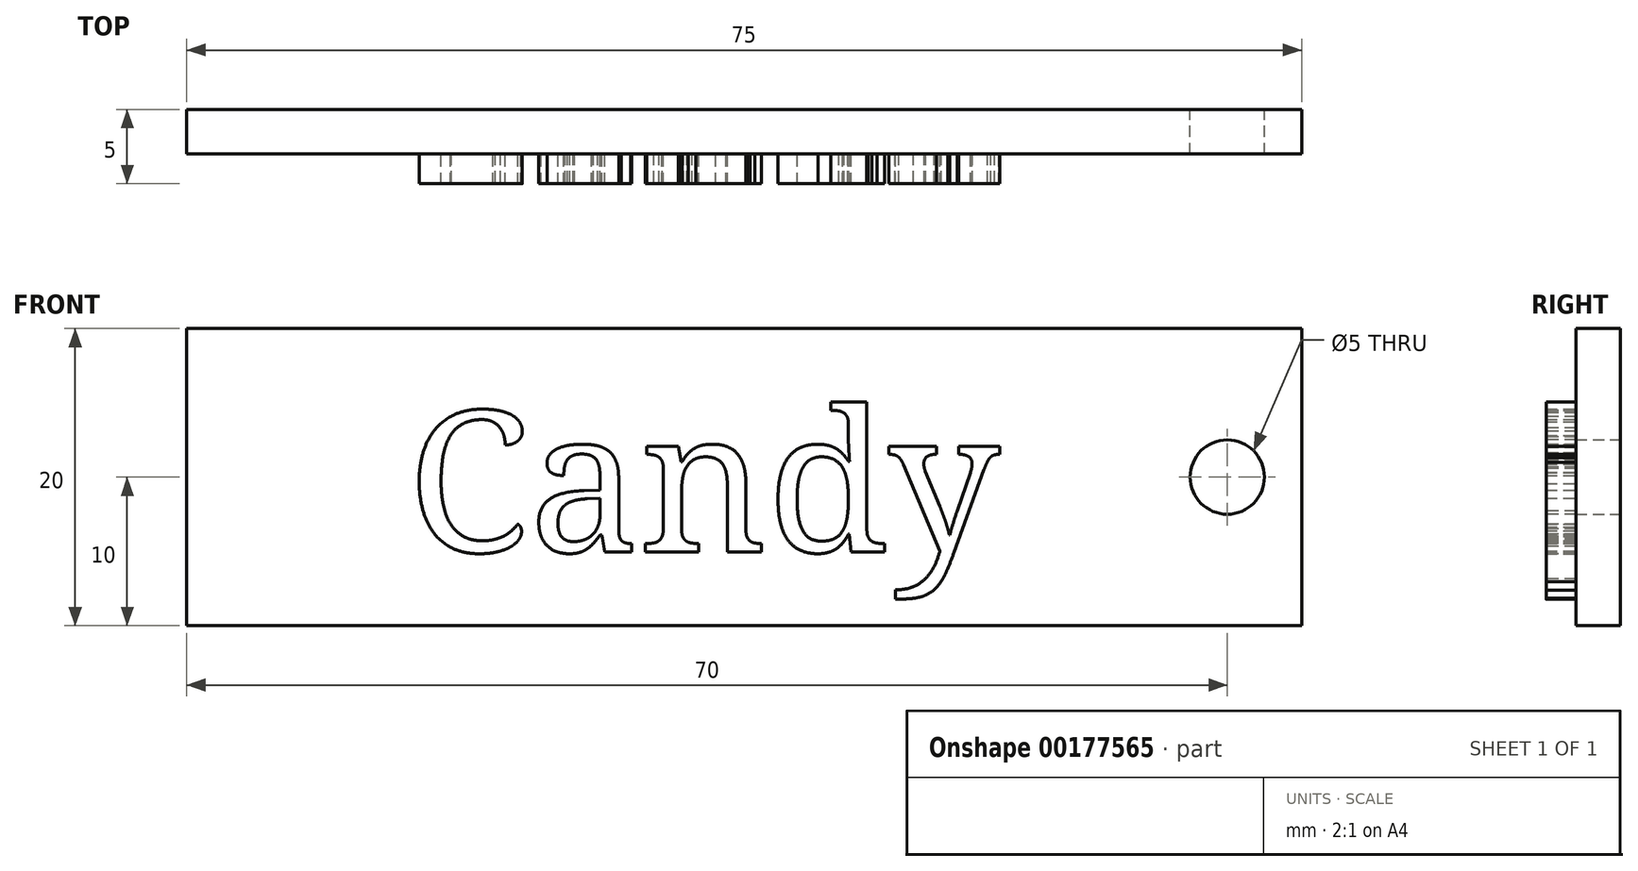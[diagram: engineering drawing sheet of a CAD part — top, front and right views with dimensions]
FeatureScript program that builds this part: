
annotation { "Feature Type Name" : "Feature", "Feature Type Description" : "" }
export const myFeature = defineFeature(function(context is Context, id is Id, definition is map)
    precondition{}
    {
        {
            var Q0;
            Q0=qCreatedBy(makeId("Front.planeOp"),FACE);
            var sketch = newSketch(context, id + "F0", { "sketchPlane" : qUnion([Q0])});
            skLineSegment(sketch, "E0.bottom", {"start": v(0, 0) * mm, "end": v(75, 0) * mm});
            skLineSegment(sketch, "E0.top", {"start": v(0, -20) * mm, "end": v(75, -20) * mm});
            skLineSegment(sketch, "E0.left", {"start": v(0, 0) * mm, "end": v(0, -20) * mm});
            skLineSegment(sketch, "E0.right", {"start": v(75, 0) * mm, "end": v(75, -20) * mm});
            skCircle(sketch, "E1", {"center": v(70, -10) * mm, "radius": 2.5 * mm});
            skSolve(sketch);
        }
        {
            var Q0;
            Q0=makeQuery(id+"F0.imprint","IMPRINT",FACE,{"disambiguationData":[TD([[makeQuery(id+"F0.imprint","IMPRINT",EDGE,{"derivedFrom":sQuery(id+"F0.wireOp",EDGE,"E0.bottom")}),-1.0]])]});
            extrude(context, id + "F1", {"entities" : qUnion([Q0]), "depth" : 3 * mm});
        }
        {
            var Q0;
            Q0=qCreatedBy(makeId("Front.planeOp"),FACE);
            var sketch = newSketch(context, id + "F2", { "sketchPlane" : qUnion([Q0])});
            skText(sketch, "E2", { "text": "Candy", "fontName": "NotoSerif-Regular.ttf"});
            const initialGuessF2  = {"E2": [0.01488, -0.01503, 1, 0, 0.00955]};
            skSetInitialGuess(sketch, initialGuessF2);
            skSolve(sketch);
        }
        {
            var Q0;
            Q0 = qSketchRegion(id + "F2", true);
            extrude(context, id + "F3", {"entities" : qUnion([Q0]), "operationType" : NewBodyOperationType.ADD, "depth" : 5 * mm});
        }
    });
